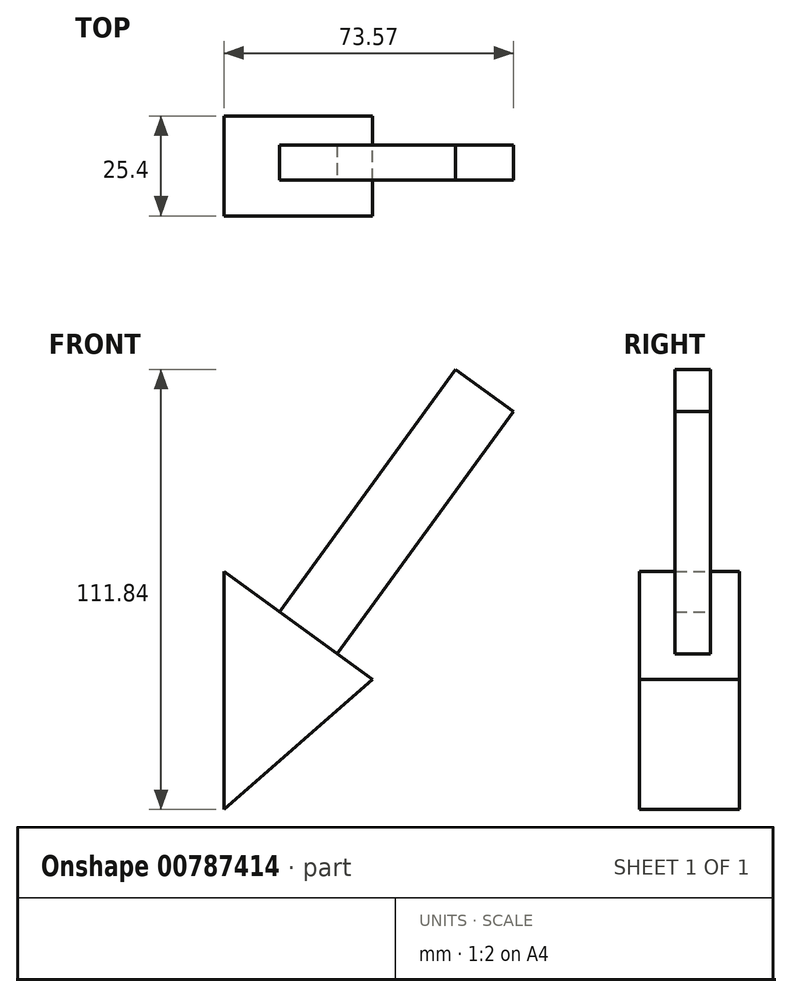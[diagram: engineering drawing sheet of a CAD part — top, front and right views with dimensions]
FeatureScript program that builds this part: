
annotation { "Feature Type Name" : "Feature", "Feature Type Description" : "" }
export const myFeature = defineFeature(function(context is Context, id is Id, definition is map)
    precondition{}
    {
        {
            var Q0;
            Q0=qCreatedBy(makeId("Front.planeOp"),FACE);
            var sketch = newSketch(context, id + "F0", { "sketchPlane" : qUnion([Q0])});
            skLineSegment(sketch, "E0", {"start": v(0, 60.49) * mm, "end": v(0, 0) * mm});
            skLineSegment(sketch, "E1", {"start": v(0, 0) * mm, "end": v(37.7, 33.07) * mm});
            skLineSegment(sketch, "E2", {"start": v(37.7, 33.07) * mm, "end": v(0, 60.49) * mm});
            skSolve(sketch);
        }
        {
            var Q0;
            Q0=makeQuery(id+"F0.imprint","IMPRINT",FACE,{"disambiguationData":[TD([[makeQuery(id+"F0.imprint","IMPRINT",EDGE,{"derivedFrom":sQuery(id+"F0.wireOp",EDGE,"E0")}),1.0]])]});
            extrude(context, id + "F1", {"entities" : qUnion([Q0]), "depth" : 25.4 * mm, "offsetDistance" : 25.4 * mm});
        }
        {
            var Q0;
            Q0=makeQuery(id+"F1.opExtrude","SWEPT_FACE",FACE,{"disambiguationData":[OSD([sQuery(id+"F0.wireOp",EDGE,"E2")])]});
            var sketch = newSketch(context, id + "F2", { "sketchPlane" : qUnion([Q0])});
            skLineSegment(sketch, "E3", {"start": v(-18.2, -7.4) * mm, "end": v(0, -7.4) * mm});
            skLineSegment(sketch, "E4", {"start": v(0, -7.4) * mm, "end": v(0, -16.35) * mm});
            skLineSegment(sketch, "E5", {"start": v(0, -16.35) * mm, "end": v(-18.2, -16.35) * mm});
            skLineSegment(sketch, "E6", {"start": v(-18.2, -16.35) * mm, "end": v(-18.2, -7.4) * mm});
            skSolve(sketch);
        }
        {
            var Q0;
            Q0=makeQuery(id+"F2.imprint","IMPRINT",FACE,{"disambiguationData":[TD([[makeQuery(id+"F2.imprint","IMPRINT",EDGE,{"derivedFrom":sQuery(id+"F2.wireOp",EDGE,"E3")}),-1.0]])]});
            extrude(context, id + "F3", {"entities" : qUnion([Q0]), "operationType" : NewBodyOperationType.ADD, "depth" : 76.15 * mm, "offsetDistance" : 25.4 * mm});
        }
    });
